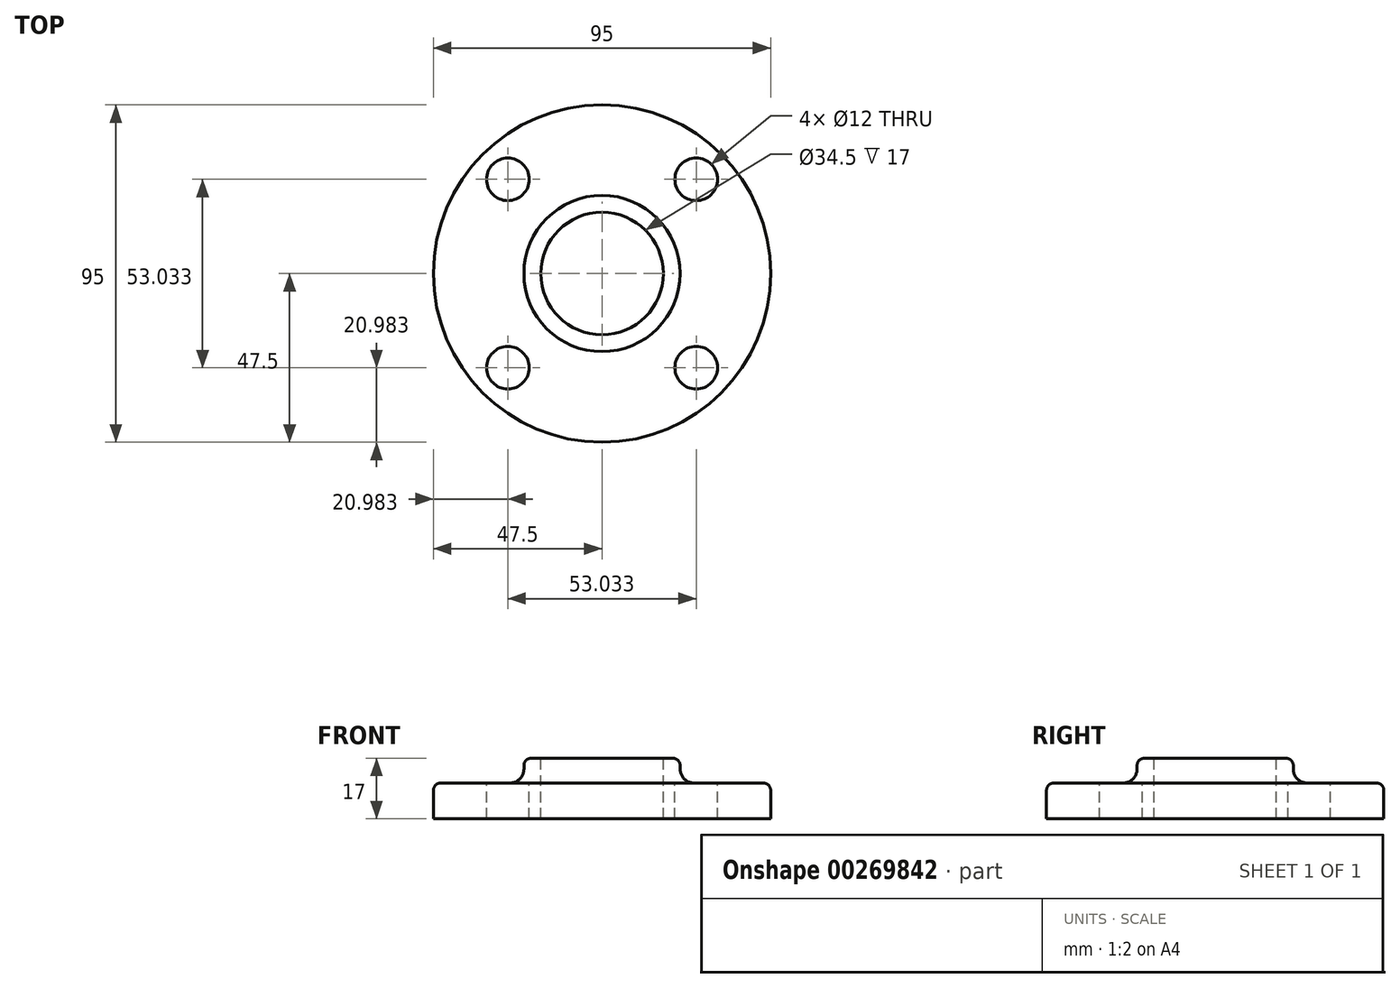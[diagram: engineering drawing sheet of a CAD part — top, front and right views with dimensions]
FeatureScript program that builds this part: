
annotation { "Feature Type Name" : "Feature", "Feature Type Description" : "" }
export const myFeature = defineFeature(function(context is Context, id is Id, definition is map)
    precondition{}
    {
        {
            var Q0;
            Q0=qCreatedBy(makeId("Front.planeOp"),FACE);
            var sketch = newSketch(context, id + "F0", { "sketchPlane" : qUnion([Q0])});
            skLineSegment(sketch, "E0", {"start": v(17.25, 17) * mm, "end": v(22, 17) * mm});
            skLineSegment(sketch, "E1", {"start": v(22, 17) * mm, "end": v(22, 10) * mm});
            skLineSegment(sketch, "E2", {"start": v(22, 10) * mm, "end": v(47.5, 10) * mm});
            skLineSegment(sketch, "E3", {"start": v(47.5, 10) * mm, "end": v(47.5, 0) * mm});
            skLineSegment(sketch, "E4", {"start": v(47.5, 0) * mm, "end": v(17.25, 0) * mm});
            skLineSegment(sketch, "E5", {"start": v(0, 23.17) * mm, "end": v(0, -14.37) * mm, "construction": true});
            skLineSegment(sketch, "E6", {"start": v(17.25, 17) * mm, "end": v(17.25, 0) * mm});
            skSolve(sketch);
        }
        {
            var Q0;
            Q0=makeQuery(id+"F0.imprint","IMPRINT",FACE,{"disambiguationData":[TD([[makeQuery(id+"F0.imprint","IMPRINT",EDGE,{"derivedFrom":sQuery(id+"F0.wireOp",EDGE,"E0")}),-1.0]])]});
            var Q1;
            Q1=sQuery(id+"F0.wireOp",EDGE,"E5");
            revolve(context, id + "F1", {"entities" : qUnion([Q0]), "axis" : qUnion([Q1]), "revolveType" : RevolveType.FULL});
        }
        {
            var Q0;
            Q0=makeQuery(id+"F1.opRevolve","SWEPT_FACE",FACE,{"disambiguationData":[OSD([sQuery(id+"F0.wireOp",EDGE,"E2")])]});
            var sketch = newSketch(context, id + "F2", { "sketchPlane" : qUnion([Q0])});
            skLineSegment(sketch, "E7", {"start": v(0, 0) * mm, "end": v(26.52, 26.52) * mm});
            skLineSegment(sketch, "E8.1.0", {"start": v(0, 0) * mm, "end": v(-26.52, 26.52) * mm});
            skLineSegment(sketch, "E8.2.0", {"start": v(0, 0) * mm, "end": v(-26.52, -26.52) * mm});
            skLineSegment(sketch, "E8.3.0", {"start": v(0, 0) * mm, "end": v(26.52, -26.52) * mm});
            skPoint(sketch, "E8.center", {"position": v(0, 0) * mm});
            skSolve(sketch);
        }
        {
            var Q0;
            Q0=sQuery(id+"F2.wireOp",VERTEX,"E8.1.0.end");
            var Q1;
            Q1=sQuery(id+"F2.wireOp",VERTEX,"E8.2.0.end");
            var Q2;
            Q2=sQuery(id+"F2.wireOp",VERTEX,"E8.3.0.end");
            var Q3;
            Q3=sQuery(id+"F2.wireOp",VERTEX,"E7.end");
            var Q4;
            Q4=makeQuery(id+"F1.opRevolve","SWEPT_BODY",BODY,{"disambiguationData":[OSD([sQuery(id+"F0.wireOp",EDGE,"E0"),sQuery(id+"F0.wireOp",EDGE,"E1"),sQuery(id+"F0.wireOp",EDGE,"E2"),sQuery(id+"F0.wireOp",EDGE,"E3"),sQuery(id+"F0.wireOp",EDGE,"E4"),sQuery(id+"F0.wireOp",EDGE,"E6")])]});
            hole(context, id + "F3", {"style" : HoleStyle.SIMPLE, "endStyle" : HoleEndStyle.THROUGH, "holeDiameter" : 12 * mm, "tappedDepth" : 12 * mm, "tapClearance" : 3, "locations" : qUnion([Q0, Q1, Q2, Q3]), "scope" : qUnion([Q4])});
        }
        {
            var Q0;
            Q0=makeQuery(id+"F1.opRevolve","SWEPT_EDGE",EDGE,{"disambiguationData":[OSD([sQuery(id+"F0.wireOp",EDGE,"E0"),sQuery(id+"F0.wireOp",EDGE,"E1")])]});
            var Q1;
            Q1=makeQuery(id+"F1.opRevolve","SWEPT_EDGE",EDGE,{"disambiguationData":[OSD([sQuery(id+"F0.wireOp",EDGE,"E2"),sQuery(id+"F0.wireOp",EDGE,"E3")])]});
            fillet(context, id + "F4", {"entities" : qUnion([Q0, Q1]), "radius" : 2 * mm, "tangentPropagation" : true, "allowEdgeOverflow" : false});
        }
        {
            var Q0;
            Q0=makeQuery(id+"F1.opRevolve","SWEPT_EDGE",EDGE,{"disambiguationData":[OSD([sQuery(id+"F0.wireOp",EDGE,"E1"),sQuery(id+"F0.wireOp",EDGE,"E2")])]});
            fillet(context, id + "F5", {"entities" : qUnion([Q0]), "radius" : 4 * mm, "tangentPropagation" : true, "allowEdgeOverflow" : false});
        }
    });
